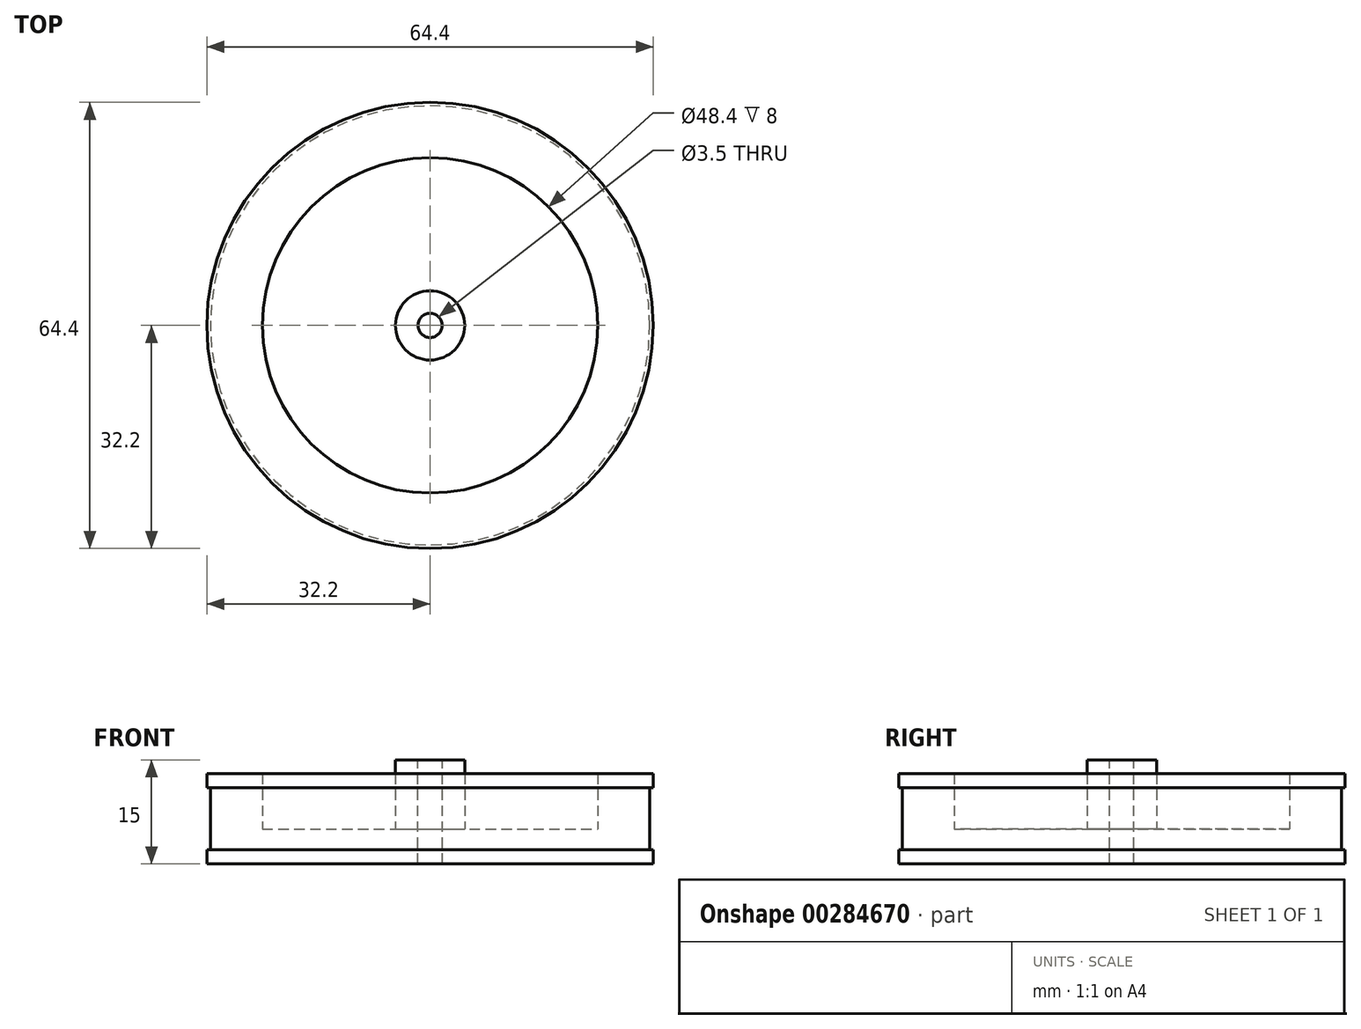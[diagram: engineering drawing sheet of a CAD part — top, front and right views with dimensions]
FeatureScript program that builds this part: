
annotation { "Feature Type Name" : "Feature", "Feature Type Description" : "" }
export const myFeature = defineFeature(function(context is Context, id is Id, definition is map)
    precondition{}
    {
        {
            var Q0;
            Q0=qCreatedBy(makeId("Front.planeOp"),FACE);
            var sketch = newSketch(context, id + "F0", { "sketchPlane" : qUnion([Q0])});
            skLineSegment(sketch, "E0", {"start": v(0, 0) * mm, "end": v(32.2, 0) * mm});
            skLineSegment(sketch, "E1", {"start": v(32.2, 0) * mm, "end": v(32.2, 2) * mm});
            skLineSegment(sketch, "E2", {"start": v(32.2, 2) * mm, "end": v(31.7, 2) * mm});
            skLineSegment(sketch, "E3", {"start": v(31.7, 2) * mm, "end": v(31.7, 11) * mm});
            skLineSegment(sketch, "E4", {"start": v(31.7, 11) * mm, "end": v(32.2, 11) * mm});
            skLineSegment(sketch, "E5", {"start": v(32.2, 11) * mm, "end": v(32.2, 13) * mm});
            skLineSegment(sketch, "E6", {"start": v(32.2, 13) * mm, "end": v(24.2, 13) * mm});
            skLineSegment(sketch, "E7", {"start": v(24.2, 13) * mm, "end": v(24.2, 5) * mm});
            skLineSegment(sketch, "E8", {"start": v(24.2, 5) * mm, "end": v(0, 5) * mm});
            skLineSegment(sketch, "E9", {"start": v(0, 0) * mm, "end": v(0, 5) * mm});
            skLineSegment(sketch, "E10", {"start": v(0, 5) * mm, "end": v(0, 15) * mm});
            skLineSegment(sketch, "E11", {"start": v(0, 15) * mm, "end": v(5, 15) * mm});
            skLineSegment(sketch, "E12", {"start": v(5, 15) * mm, "end": v(5, 5) * mm});
            skSolve(sketch);
        }
        {
            var Q0;
            {var subQ0=sQuery(id+"F0.wireOp",EDGE,"E10");Q0=makeQuery(id+"F0.imprint","IMPRINT",FACE,{"disambiguationData":[TD([[makeQuery(id+"F0.imprint","IMPRINT",EDGE,{"derivedFrom":subQ0}),-1.0]])]});}
            var Q1;
            Q1=makeQuery(id+"F0.imprint","IMPRINT",FACE,{"disambiguationData":[TD([[makeQuery(id+"F0.imprint","IMPRINT",EDGE,{"derivedFrom":sQuery(id+"F0.wireOp",EDGE,"E0")}),1.0]])]});
            var Q2;
            Q2=sQuery(id+"F0.wireOp",EDGE,"E10");
            revolve(context, id + "F1", {"entities" : qUnion([Q0, Q1]), "axis" : qUnion([Q2]), "revolveType" : RevolveType.FULL});
        }
        {
            var Q0;
            Q0=makeQuery(id+"F1.opRevolve","SWEPT_FACE",FACE,{"disambiguationData":[OSD([sQuery(id+"F0.wireOp",EDGE,"E11")])]});
            var sketch = newSketch(context, id + "F2", { "sketchPlane" : qUnion([Q0])});
            skSolve(sketch);
        }
        {
            var Q0;
            Q0=makeQuery(id+"F2.imprint","IMPRINT",FACE,{"disambiguationData":[TD([[makeQuery(id+"F2.imprint","IMPRINT",EDGE,{"derivedFrom":makeQuery(id+"F1.opRevolve","SWEPT_EDGE",EDGE,{"disambiguationData":[OSD([sQuery(id+"F0.wireOp",EDGE,"E11"),sQuery(id+"F0.wireOp",EDGE,"E12")])]})}),-1.0]])]});
            var sketch = newSketch(context, id + "F3", { "sketchPlane" : qUnion([Q0])});
            skCircle(sketch, "E13.0.0", {"center": v(0, 0) * mm, "radius": 5 * mm});
            skCircle(sketch, "E14", {"center": v(0, 0) * mm, "radius": 1.75 * mm});
            skSolve(sketch);
        }
        {
            var Q0;
            Q0=makeQuery(id+"F3.imprint","IMPRINT",FACE,{"disambiguationData":[TD([[makeQuery(id+"F3.imprint","IMPRINT",EDGE,{"derivedFrom":sQuery(id+"F3.wireOp",EDGE,"E14")}),1.0]])]});
            extrude(context, id + "F4", {"entities" : qUnion([Q0]), "operationType" : NewBodyOperationType.REMOVE, "oppositeDirection" : true, "depth" : 40 * mm});
        }
    });
